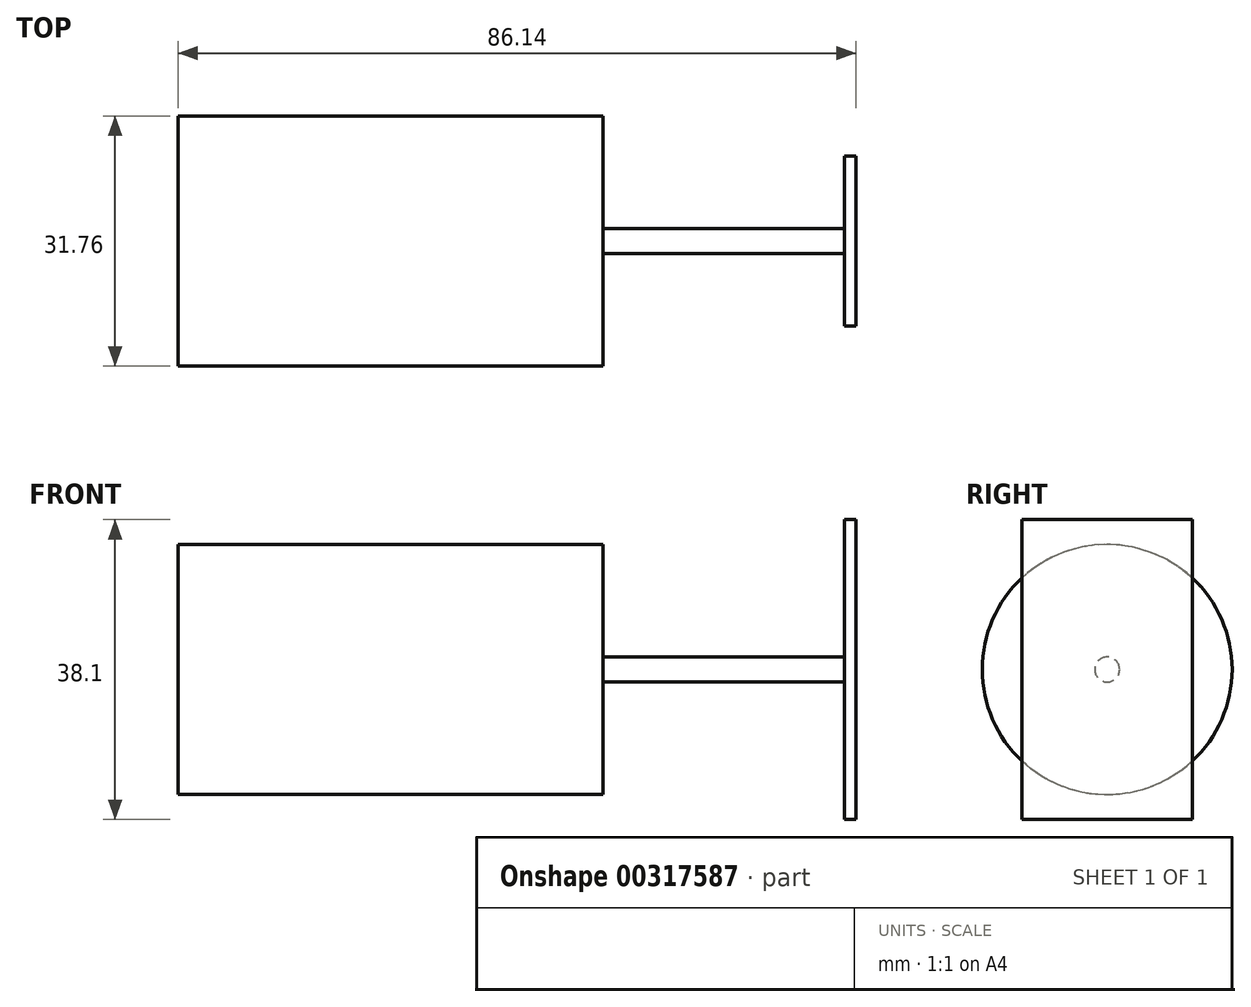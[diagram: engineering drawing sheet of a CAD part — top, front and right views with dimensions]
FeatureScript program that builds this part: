
annotation { "Feature Type Name" : "Feature", "Feature Type Description" : "" }
export const myFeature = defineFeature(function(context is Context, id is Id, definition is map)
    precondition{}
    {
        {
            var Q0;
            Q0=qCreatedBy(makeId("Right.planeOp"),FACE);
            var sketch = newSketch(context, id + "F0", { "sketchPlane" : qUnion([Q0])});
            skCircle(sketch, "E0", {"center": v(0, 0) * mm, "radius": 15.88 * mm});
            skSolve(sketch);
        }
        {
            var Q0;
            Q0=makeQuery(id+"F0.imprint","IMPRINT",FACE,{"disambiguationData":[TD([[makeQuery(id+"F0.imprint","IMPRINT",EDGE,{"derivedFrom":sQuery(id+"F0.wireOp",EDGE,"E0")}),1.0]])]});
            extrude(context, id + "F1", {"entities" : qUnion([Q0]), "endBound" : BoundingType.SYMMETRIC, "depth" : 53.97 * mm});
        }
        {
            var Q0;
            Q0=makeQuery(id+"F1.opExtrude","CAP_FACE",FACE,{"disambiguationData":[OSD([sQuery(id+"F0.wireOp",EDGE,"E0")])],"isStart":false});
            var sketch = newSketch(context, id + "F2", { "sketchPlane" : qUnion([Q0])});
            skCircle(sketch, "E1", {"center": v(0, 0) * mm, "radius": 1.59 * mm});
            skSolve(sketch);
        }
        {
            var Q0;
            Q0=makeQuery(id+"F2.imprint","IMPRINT",FACE,{"disambiguationData":[TD([[makeQuery(id+"F2.imprint","IMPRINT",EDGE,{"derivedFrom":sQuery(id+"F2.wireOp",EDGE,"E1")}),1.0]])]});
            extrude(context, id + "F3", {"entities" : qUnion([Q0]), "operationType" : NewBodyOperationType.ADD, "depth" : 31.75 * mm});
        }
        {
            var Q0;
            Q0=qCreatedBy(makeId("Top.planeOp"),FACE);
            var sketch = newSketch(context, id + "F4", { "sketchPlane" : qUnion([Q0])});
            skLineSegment(sketch, "E2.bottom", {"start": v(59.15, 10.8) * mm, "end": v(57.68, 10.8) * mm});
            skLineSegment(sketch, "E2.top", {"start": v(59.15, -10.8) * mm, "end": v(57.68, -10.8) * mm});
            skLineSegment(sketch, "E2.left", {"start": v(59.15, 10.8) * mm, "end": v(59.15, -10.8) * mm});
            skLineSegment(sketch, "E2.right", {"start": v(57.68, 10.8) * mm, "end": v(57.68, -10.8) * mm});
            skPoint(sketch, "E2.middle", {"position": v(58.41, 0) * mm});
            skSolve(sketch);
        }
        {
            var Q0;
            Q0=makeQuery(id+"F4.imprint","IMPRINT",FACE,{"disambiguationData":[TD([[makeQuery(id+"F4.imprint","IMPRINT",EDGE,{"derivedFrom":sQuery(id+"F4.wireOp",EDGE,"E2.bottom")}),1.0]])]});
            extrude(context, id + "F5", {"entities" : qUnion([Q0]), "operationType" : NewBodyOperationType.ADD, "endBound" : BoundingType.SYMMETRIC, "depth" : 38.1 * mm});
        }
    });
